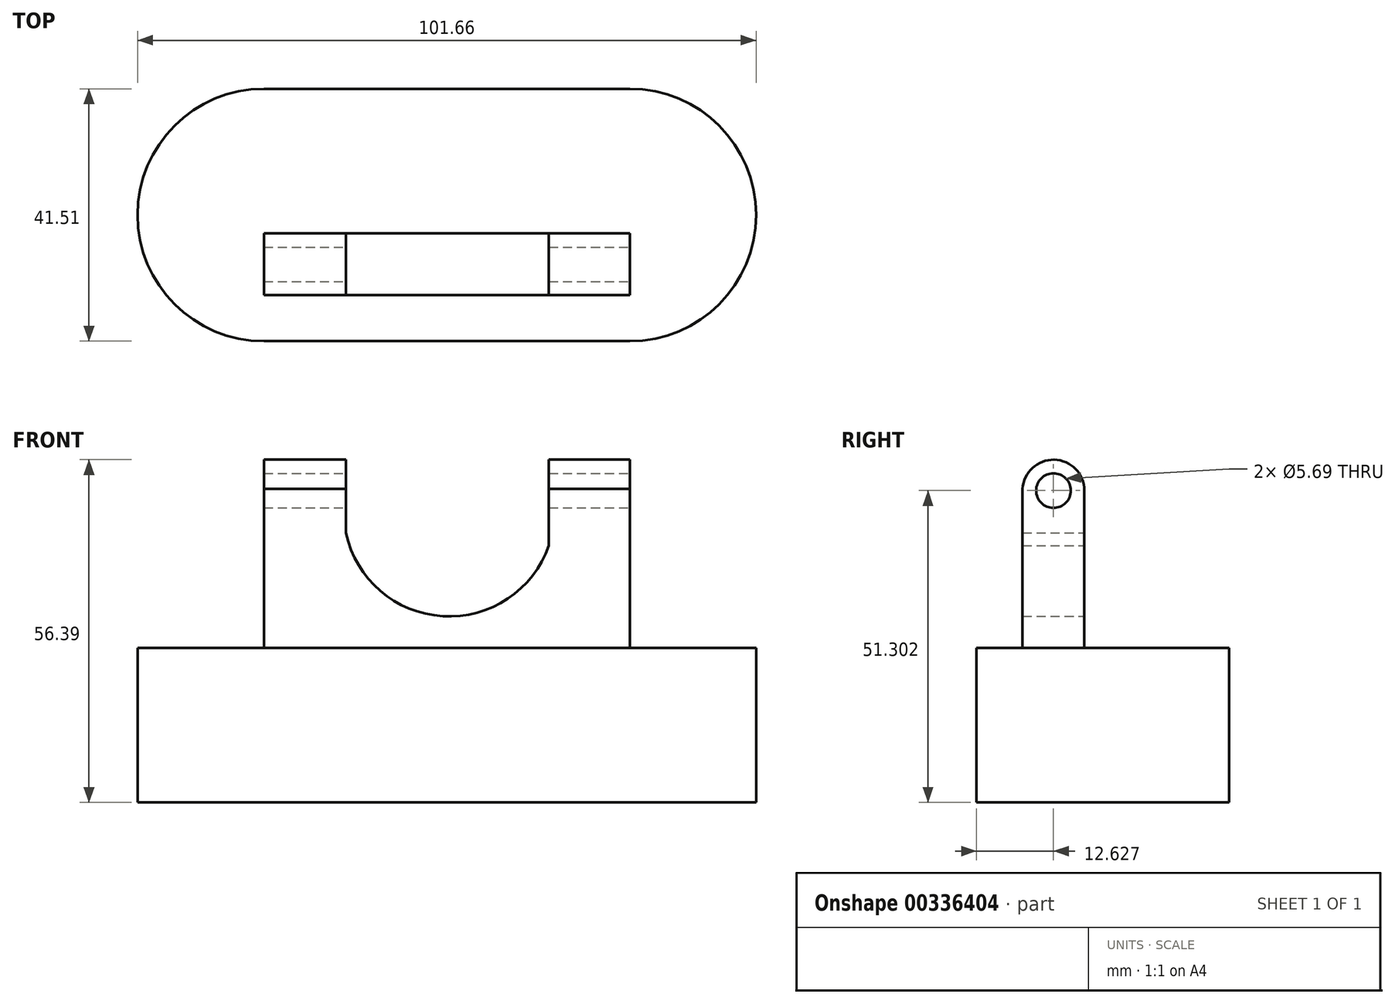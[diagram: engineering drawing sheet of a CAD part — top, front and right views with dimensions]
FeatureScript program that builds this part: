
annotation { "Feature Type Name" : "Feature", "Feature Type Description" : "" }
export const myFeature = defineFeature(function(context is Context, id is Id, definition is map)
    precondition{}
    {
        {
            var Q0;
            Q0=qCreatedBy(makeId("Top.planeOp"),FACE);
            var sketch = newSketch(context, id + "F0", { "sketchPlane" : qUnion([Q0])});
            skLineSegment(sketch, "E0", {"start": v(-30.38, 28.88) * mm, "end": v(29.78, 28.88) * mm});
            skLineSegment(sketch, "E1", {"start": v(-30.38, -12.63) * mm, "end": v(29.78, -12.63) * mm});
            skArc(sketch, "E2", {"start": v(29.78, 28.88) * mm, "mid": v(50.53, 8.12) * mm, "end": v(29.78, -12.63) * mm});
            skArc(sketch, "E3", {"start": v(-30.38, 28.88) * mm, "mid": v(-51.13, 8.12) * mm, "end": v(-30.38, -12.63) * mm});
            skSolve(sketch);
        }
        {
            var Q0;
            Q0 = qSketchRegion(id + "F0", true);
            extrude(context, id + "F1", {"entities" : qUnion([Q0]), "depth" : 25.4 * mm});
        }
        {
            var Q0;
            Q0=qCreatedBy(makeId("Front.planeOp"),FACE);
            var sketch = newSketch(context, id + "F2", { "sketchPlane" : qUnion([Q0])});
            skLineSegment(sketch, "E4.0", {"start": v(-30.38, 25.4) * mm, "end": v(29.78, 25.4) * mm});
            skLineSegment(sketch, "E5.0", {"start": v(-30.38, 25.4) * mm, "end": v(-51.13, 25.4) * mm});
            skLineSegment(sketch, "E6", {"start": v(50.53, 25.4) * mm, "end": v(50.53, 0) * mm});
            skLineSegment(sketch, "E7.0", {"start": v(29.78, 25.4) * mm, "end": v(50.53, 25.4) * mm});
            skLineSegment(sketch, "E8", {"start": v(-30.38, 25.4) * mm, "end": v(-30.38, 59.54) * mm});
            skLineSegment(sketch, "E9", {"start": v(-30.38, 59.54) * mm, "end": v(-17.01, 59.54) * mm});
            skLineSegment(sketch, "E10", {"start": v(29.78, 25.4) * mm, "end": v(29.78, 59.54) * mm});
            skLineSegment(sketch, "E11", {"start": v(29.78, 59.54) * mm, "end": v(15.95, 59.54) * mm});
            skArc(sketch, "E12", {"start": v(-17.01, 59.54) * mm, "mid": v(-0.53, 43.42) * mm, "end": v(15.95, 59.54) * mm});
            skSolve(sketch);
        }
        {
            var Q0;
            Q0 = qSketchRegion(id + "F2", true);
            extrude(context, id + "F3", {"entities" : qUnion([Q0]), "operationType" : NewBodyOperationType.ADD, "oppositeDirection" : true, "depth" : 5.08 * mm});
        }
        {
            var Q0;
            Q0=makeQuery(id+"F3.opExtrude","CAP_FACE",FACE,{"disambiguationData":[OSD([sQuery(id+"F2.wireOp",EDGE,"E4.0"),sQuery(id+"F2.wireOp",EDGE,"E8"),sQuery(id+"F2.wireOp",EDGE,"E9"),sQuery(id+"F2.wireOp",EDGE,"E10"),sQuery(id+"F2.wireOp",EDGE,"E11"),sQuery(id+"F2.wireOp",EDGE,"E12")])],"isStart":true});
            var sketch = newSketch(context, id + "F4", { "sketchPlane" : qUnion([Q0])});
            skLineSegment(sketch, "E13.0.0", {"start": v(-30.38, 25.4) * mm, "end": v(29.78, 25.4) * mm});
            skLineSegment(sketch, "E13.0.1", {"start": v(29.78, 25.4) * mm, "end": v(29.78, 59.54) * mm});
            skLineSegment(sketch, "E13.0.2", {"start": v(29.78, 59.54) * mm, "end": v(15.95, 59.54) * mm});
            skArc(sketch, "E13.0.3", {"start": v(15.95, 59.54) * mm, "mid": v(-0.53, 43.42) * mm, "end": v(-17.01, 59.54) * mm});
            skLineSegment(sketch, "E13.0.4", {"start": v(-17.01, 59.54) * mm, "end": v(-30.38, 59.54) * mm});
            skLineSegment(sketch, "E13.0.5", {"start": v(-30.38, 59.54) * mm, "end": v(-30.38, 25.4) * mm});
            skSolve(sketch);
        }
        {
            var Q0;
            Q0 = qSketchRegion(id + "F4", true);
            var Q1;
            Q1=makeQuery(id+"F4.imprint","IMPRINT",FACE,{"disambiguationData":[TD([[makeQuery(id+"F4.imprint","IMPRINT",EDGE,{"derivedFrom":sQuery(id+"F4.wireOp",EDGE,"E13.0.0")}),1.0]])]});
            extrude(context, id + "F5", {"entities" : qUnion([Q0, Q1]), "operationType" : NewBodyOperationType.ADD, "depth" : 5.08 * mm});
        }
        {
            var Q0;
            Q0=makeQuery(id+"F5.boolean.opBoolean","MERGE",FACE,{"derivedFrom":[makeQuery(id+"F3.opExtrude","SWEPT_FACE",FACE,{"disambiguationData":[OSD([sQuery(id+"F2.wireOp",EDGE,"E10")])]}),makeQuery(id+"F5.opExtrude","SWEPT_FACE",FACE,{"disambiguationData":[OSD([sQuery(id+"F4.wireOp",EDGE,"E13.0.1")])]})]});
            var sketch = newSketch(context, id + "F6", { "sketchPlane" : qUnion([Q0])});
            skLineSegment(sketch, "E14.0.0", {"start": v(5.08, 59.54) * mm, "end": v(-5.08, 59.54) * mm});
            skLineSegment(sketch, "E14.0.1", {"start": v(-5.08, 59.54) * mm, "end": v(-5.08, 25.4) * mm});
            skLineSegment(sketch, "E14.0.2", {"start": v(-5.08, 25.4) * mm, "end": v(5.08, 25.4) * mm});
            skLineSegment(sketch, "E14.0.3", {"start": v(5.08, 25.4) * mm, "end": v(5.08, 59.54) * mm});
            skArc(sketch, "E15", {"start": v(5.08, 51.3) * mm, "mid": v(0.13, 56.36) * mm, "end": v(-5.08, 51.57) * mm});
            skLineSegment(sketch, "E16", {"start": v(-5.08, 51.57) * mm, "end": v(-5.08, 59.54) * mm});
            skLineSegment(sketch, "E17", {"start": v(5.08, 59.54) * mm, "end": v(5.08, 51.3) * mm});
            skLineSegment(sketch, "E18", {"start": v(-5.08, 59.54) * mm, "end": v(5.08, 59.54) * mm});
            skArc(sketch, "E19", {"start": v(5.08, 51.3) * mm, "mid": v(0.13, 56.38) * mm, "end": v(-5.08, 51.57) * mm});
            skSolve(sketch);
        }
        {
            var Q0;
            Q0=makeQuery(id+"F6.imprint","IMPRINT",FACE,{"disambiguationData":[TD([[makeQuery(id+"F6.imprint","IMPRINT",EDGE,{"derivedFrom":sQuery(id+"F6.wireOp",EDGE,"E19")}),-1.0]])]});
            extrude(context, id + "F7", {"entities" : qUnion([Q0]), "operationType" : NewBodyOperationType.REMOVE, "endBound" : BoundingType.THROUGH_ALL, "oppositeDirection" : true, "depth" : 25.4 * mm});
        }
        {
            var Q0;
            Q0=makeQuery(id+"F5.boolean.opBoolean","MERGE",FACE,{"derivedFrom":[makeQuery(id+"F3.opExtrude","SWEPT_FACE",FACE,{"disambiguationData":[OSD([sQuery(id+"F2.wireOp",EDGE,"E10")])]}),makeQuery(id+"F5.opExtrude","SWEPT_FACE",FACE,{"disambiguationData":[OSD([sQuery(id+"F4.wireOp",EDGE,"E13.0.1")])]})]});
            var sketch = newSketch(context, id + "F8", { "sketchPlane" : qUnion([Q0])});
            skArc(sketch, "E20.0", {"start": v(5.08, 51.3) * mm, "mid": v(0.13, 56.38) * mm, "end": v(-5.08, 51.57) * mm});
            skCircle(sketch, "E21", {"center": v(0, 51.3) * mm, "radius": 2.85 * mm});
            skSolve(sketch);
        }
        {
            var Q0;
            Q0 = qSketchRegion(id + "F8", true);
            extrude(context, id + "F9", {"entities" : qUnion([Q0]), "operationType" : NewBodyOperationType.REMOVE, "endBound" : BoundingType.THROUGH_ALL, "oppositeDirection" : true, "depth" : 25.4 * mm});
        }
        {
            var Q0;
            Q0=qCreatedBy(makeId("Front.planeOp"),FACE);
            var sketch = newSketch(context, id + "F10", { "sketchPlane" : qUnion([Q0])});
            skLineSegment(sketch, "E22", {"start": v(16.47, 56.39) * mm, "end": v(29.78, 56.39) * mm});
            skLineSegment(sketch, "E23", {"start": v(-30.38, 56.39) * mm, "end": v(-16.87, 56.39) * mm});
            skLineSegment(sketch, "E24", {"start": v(16.47, 56.39) * mm, "end": v(16.47, 42.28) * mm});
            skLineSegment(sketch, "E25", {"start": v(-16.87, 56.39) * mm, "end": v(-16.87, 44.33) * mm});
            skArc(sketch, "E26", {"start": v(-16.87, 44.33) * mm, "mid": v(-0.98, 30.64) * mm, "end": v(16.47, 42.28) * mm});
            skLineSegment(sketch, "E27", {"start": v(16.47, 56.39) * mm, "end": v(-16.87, 56.39) * mm});
            skSolve(sketch);
        }
        {
            var Q0;
            Q0 = qSketchRegion(id + "F10", true);
            extrude(context, id + "F11", {"entities" : qUnion([Q0]), "operationType" : NewBodyOperationType.REMOVE, "depth" : 25.4 * mm});
        }
        {
            var Q0;
            Q0 = qSketchRegion(id + "F10", true);
            extrude(context, id + "F12", {"entities" : qUnion([Q0]), "operationType" : NewBodyOperationType.REMOVE, "oppositeDirection" : true, "depth" : 25.4 * mm});
        }
    });
